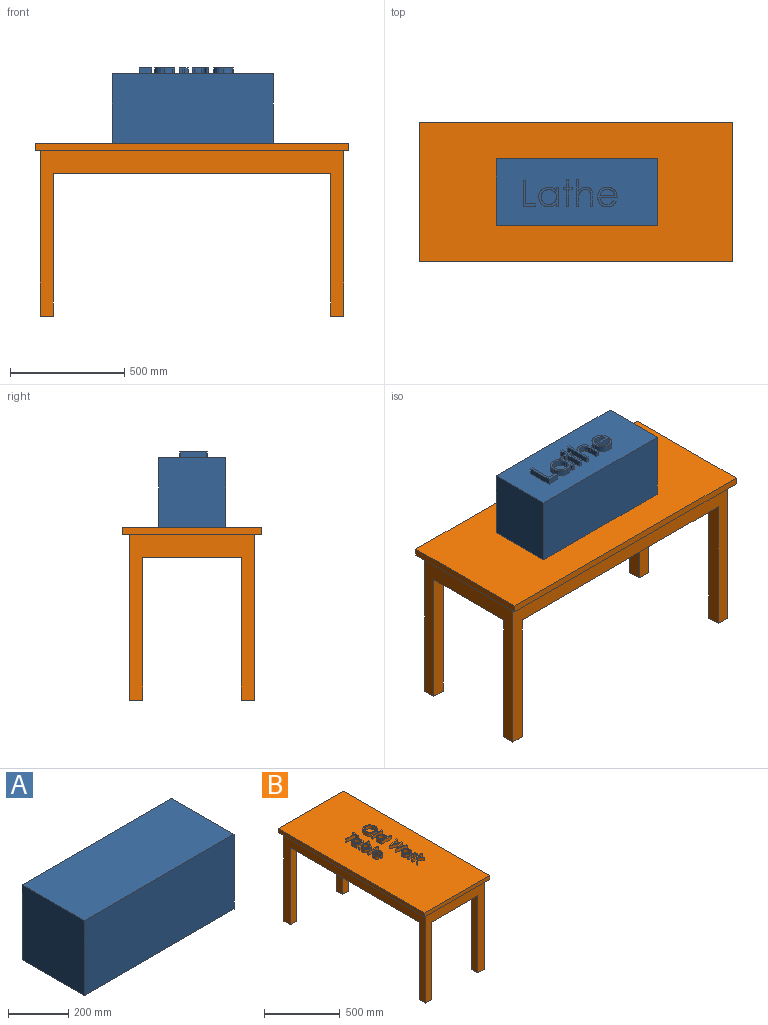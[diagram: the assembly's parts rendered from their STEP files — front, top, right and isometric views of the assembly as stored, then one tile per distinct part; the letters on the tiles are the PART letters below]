
ASSEMBLY  parts=2 mates=1
PART A: 72 faces, bbox 704.9x292.1x330.2 mm
  f0: plane 704.85x292.1mm, normal (0,0,-1), area 189595.3mm2, adj f1,f2,f3,f4,f6,f7,f8,f9
  f1: plane 304.8x292.1mm, normal (-1,0,0), area 89032.1mm2, adj f0,f2,f4,f5
  f2: plane 704.85x304.8mm, normal (0,1,0), area 214838.3mm2, adj f0,f1,f3,f5
  f3: plane 304.8x292.1mm, normal (1,0,0), area 89032.1mm2, adj f0,f2,f4,f5
  f4: plane 704.85x304.8mm, normal (0,-1,0), area 214838.3mm2, adj f0,f1,f3,f5
  f5: plane 704.85x292.1mm, normal (0,0,1), area 205886.7mm2, adj f1,f2,f3,f4
  f6: plane 114.3x25.4mm, normal (-1,0,0), area 2903.2mm2, adj f0,f7,f11,f12
  f7: plane 54.22x25.4mm, normal (0,1,0), area 1377.2mm2, adj f0,f6,f8,f12
  f8: plane 25.4x11.72mm, normal (1,0,0), area 297.8mm2, adj f0,f7,f9,f12
  f9: plane 43.96x25.4mm, normal (0,-1,0), area 1116.6mm2, adj f0,f8,f10,f12
  f10: plane 102.58x25.4mm, normal (1,0,0), area 2605.5mm2, adj f0,f9,f11,f12
  f11: plane 25.4x10.26mm, normal (0,-1,0), area 260.5mm2, adj f0,f6,f10,f12
  f12: plane 114.3x54.22mm, normal (0,0,-1), area 1687.8mm2, adj f6,f7,f8,f9,f10,f11
  f13: plane 87.92x86.46mm, normal (0,0,-1), area 2938.1mm2, adj f14,f15,f16,f17,f18,f19,f20,f21
  f14: plane 25.4x10.26mm, normal (0,-1,0), area 260.5mm2, adj f0,f13,f15,f22
  f15: plane 25.4x15.46mm, normal (-1,0,0), area 392.6mm2, adj f0,f13,f14,f16
  f16: extruded ~33.8x25.4mm, area 1000.4mm2, adj f0,f13,f15,f17
  f17: extruded ~43.87x43mm, area 1735.3mm2, adj f0,f13,f16,f18
  f18: extruded ~43.55x43.46mm, area 1739.5mm2, adj f0,f13,f17,f19
  f19: extruded ~34.12x25.4mm, area 990.3mm2, adj f0,f13,f18,f20
  f20: plane 25.4x14.45mm, normal (-1,0,0), area 367mm2, adj f0,f13,f19,f21
  f21: plane 25.4x10.26mm, normal (0,1,0), area 260.5mm2, adj f0,f13,f20,f22
  f22: plane 83.53x25.4mm, normal (1,0,0), area 2121.6mm2, adj f0,f13,f14,f21
  f23: extruded ~33.66x33.15mm, area 1339.9mm2, adj f13,f24,f26,f27
  f24: extruded ~33.75x32.86mm, area 1330.1mm2, adj f13,f23,f25,f27
  f25: extruded ~33.66x33.09mm, area 1330mm2, adj f13,f24,f26,f27
  f26: extruded ~33.75x32.79mm, area 1333.9mm2, adj f13,f23,f25,f27
  f27: plane 67.41x65.94mm, normal (0,0,-1), area 3508mm2, adj f23,f24,f25,f26
  f28: plane 33.7x25.4mm, normal (-1,0,0), area 856.1mm2, adj f0,f29,f39,f40
  f29: plane 25.4x14.65mm, normal (0,-1,0), area 372.2mm2, adj f0,f28,f30,f40
  f30: plane 25.4x10.26mm, normal (-1,0,0), area 260.5mm2, adj f0,f29,f31,f40
  f31: plane 25.4x14.65mm, normal (0,1,0), area 372.2mm2, adj f0,f30,f32,f40
  f32: plane 73.27x25.4mm, normal (-1,0,0), area 1861mm2, adj f0,f31,f33,f40
  f33: plane 25.4x10.26mm, normal (0,1,0), area 260.5mm2, adj f0,f32,f34,f40
  f34: plane 73.27x25.4mm, normal (1,0,0), area 1861mm2, adj f0,f33,f35,f40
  f35: plane 25.4x14.65mm, normal (0,1,0), area 372.2mm2, adj f0,f34,f36,f40
  f36: plane 25.4x10.26mm, normal (1,0,0), area 260.5mm2, adj f0,f35,f37,f40
  f37: plane 25.4x14.65mm, normal (0,-1,0), area 372.2mm2, adj f0,f36,f38,f40
  f38: plane 33.7x25.4mm, normal (1,0,0), area 856.1mm2, adj f0,f37,f39,f40
  f39: plane 25.4x10.26mm, normal (0,-1,0), area 260.5mm2, adj f0,f28,f38,f40
  f40: plane 117.23x39.57mm, normal (0,0,-1), area 1503.1mm2, adj f28,f29,f30,f31,f32,f33,f34,f35
  f41: plane 117.23x25.4mm, normal (-1,0,0), area 2977.7mm2, adj f0,f42,f54,f55
  f42: plane 25.4x10.26mm, normal (0,1,0), area 260.5mm2, adj f0,f41,f43,f55
  f43: plane 30.2x25.4mm, normal (1,0,0), area 767.1mm2, adj f0,f42,f44,f55
  f44: extruded ~25.4x22.42mm, area 571.9mm2, adj f0,f43,f45,f55
  f45: extruded ~28.39x25.4mm, area 982mm2, adj f0,f44,f46,f55
  f46: extruded ~25.4x21.59mm, area 754mm2, adj f0,f45,f47,f55
  f47: extruded ~25.4x19mm, area 484.5mm2, adj f0,f46,f48,f55
  f48: plane 39.29x25.4mm, normal (-1,0,0), area 998mm2, adj f0,f47,f49,f55
  f49: plane 25.4x10.26mm, normal (0,1,0), area 260.5mm2, adj f0,f48,f50,f55
  f50: plane 42.66x25.4mm, normal (1,0,0), area 1083.5mm2, adj f0,f49,f51,f55
  f51: extruded ~42.34x31.23mm, area 1525.1mm2, adj f0,f50,f52,f55
  f52: extruded ~31.78x25.4mm, area 954mm2, adj f0,f51,f53,f55
  f53: plane 49.48x25.4mm, normal (1,0,0), area 1256.8mm2, adj f0,f52,f54,f55
  f54: plane 25.4x10.26mm, normal (0,-1,0), area 260.5mm2, adj f0,f41,f53,f55
  f55: plane 117.23x73.27mm, normal (0,0,-1), area 2548.4mm2, adj f41,f42,f43,f44,f45,f46,f47,f48
  f56: plane 86.46x84.99mm, normal (0,0,-1), area 2916.5mm2, adj f57,f58,f59,f60,f61,f62,f63,f64
  f57: extruded ~30.75x25.4mm, area 944.5mm2, adj f0,f56,f58,f66
  f58: extruded ~30.77x30.48mm, area 1227.5mm2, adj f0,f56,f57,f59
  f59: plane 74.73x25.4mm, normal (0,1,0), area 1898.3mm2, adj f0,f56,f58,f60
  f60: extruded ~28.99x25.4mm, area 785.7mm2, adj f0,f56,f59,f61
  f61: extruded ~33.64x25.4mm, area 988.3mm2, adj f0,f56,f60,f62
  f62: extruded ~32.65x25.4mm, area 953.8mm2, adj f0,f56,f61,f63
  f63: extruded ~27.89x25.4mm, area 763.9mm2, adj f0,f56,f62,f64
  f64: extruded ~43x42.02mm, area 1708.4mm2, adj f0,f56,f63,f65
  f65: extruded ~38.58x25.4mm, area 1206.5mm2, adj f0,f56,f64,f66
  f66: plane 25.4x9.11mm, normal (0.46,-0.89,0), area 261.4mm2, adj f0,f56,f57,f65
  f67: plane 63.4x25.4mm, normal (0,-1,0), area 1610.4mm2, adj f56,f68,f70,f71
  f68: extruded ~31.94x25.4mm, area 1117.1mm2, adj f56,f67,f69,f71
  f69: extruded ~25.4x21.52mm, area 595.1mm2, adj f56,f68,f70,f71
  f70: extruded ~25.4x17.08mm, area 508.8mm2, adj f56,f67,f69,f71
  f71: plane 63.4x24.91mm, normal (0,0,-1), area 1189.4mm2, adj f67,f68,f69,f70
PART B: 163 faces, bbox 609.9x1371.7x781.1 mm
  f0: plane 1371.73x609.89mm, normal (0,0,1), area 803903mm2, adj f10,f11,f12,f13,f24,f25,f26,f27
  f1: plane 1371.73x609.89mm, normal (0,0,-1), area 111370.7mm2, adj f10,f11,f12,f13,f14,f15,f17,f19
  f2: plane 625.48x57.15mm, normal (1,0,0), area 35745.9mm2, adj f3,f14,f16,f22
  f3: plane 625.48x57.15mm, normal (0,-1,0), area 35745.9mm2, adj f2,f15,f16,f22
  f4: plane 625.48x57.15mm, normal (0,-1,0), area 35745.9mm2, adj f5,f17,f18,f22
  f5: plane 625.48x57.15mm, normal (-1,0,0), area 35745.9mm2, adj f4,f14,f18,f22
  f6: plane 625.48x57.15mm, normal (-1,0,0), area 35745.9mm2, adj f7,f19,f20,f22
  f7: plane 625.48x57.15mm, normal (0,1,0), area 35745.9mm2, adj f6,f17,f20,f22
  f8: plane 625.48x57.15mm, normal (0,1,0), area 35745.9mm2, adj f9,f15,f21,f22
  f9: plane 625.48x57.15mm, normal (1,0,0), area 35745.9mm2, adj f8,f19,f21,f22
  f10: plane 609.6x31.75mm, normal (0,1,0), area 19354.8mm2, adj f0,f1,f11,f13
  f11: plane 1371.6x31.75mm, normal (-1,0,0), area 43548.3mm2, adj f0,f1,f10,f12
  f12: plane 609.6x31.75mm, normal (0,-1,0), area 19354.8mm2, adj f0,f1,f11,f13
  f13: plane 1371.6x31.75mm, normal (1,0,0), area 43548.3mm2, adj f0,f1,f10,f12
  f14: plane 723.9x546.1mm, normal (0,1,0), area 125241.7mm2, adj f1,f2,f5,f15,f16,f17,f18,f22
  f15: plane 1327.15x723.9mm, normal (-1,0,0), area 202116.5mm2, adj f1,f3,f8,f14,f16,f19,f21,f22
  f16: plane 57.16x57.16mm, normal (0,0,-1), area 3266.1mm2, adj f2,f3,f14,f15
  f17: plane 1327.15x723.9mm, normal (1,0,0), area 202116.5mm2, adj f1,f4,f7,f14,f18,f19,f20,f22
  f18: plane 57.16x57.16mm, normal (0,0,-1), area 3266.1mm2, adj f4,f5,f14,f17
  f19: plane 723.9x546.1mm, normal (0,-1,0), area 125241.7mm2, adj f1,f6,f9,f15,f17,f20,f21,f22
  f20: plane 57.16x57.16mm, normal (0,0,-1), area 3266.1mm2, adj f6,f7,f17,f19
  f21: plane 57.16x57.16mm, normal (0,0,-1), area 3266.1mm2, adj f8,f9,f15,f19
  f22: plane 1327.24x546.36mm, normal (0,0,-1), area 711692.1mm2, adj f2,f3,f4,f5,f6,f7,f8,f9
  f23: plane 93.46x93.46mm, normal (0,0,1), area 2301.1mm2, adj f24,f25,f26,f27,f28,f29,f30,f31
  f24: extruded ~47.13x46.15mm, area 1864.4mm2, adj f0,f23,f25,f27
  f25: extruded ~46.88x46.33mm, area 1865mm2, adj f0,f23,f24,f26
  f26: extruded ~46.78x46.58mm, area 1868mm2, adj f0,f23,f25,f27
  f27: extruded ~47.31x46.68mm, area 1884.7mm2, adj f0,f23,f24,f26
  f28: extruded ~38.94x37.55mm, area 1529.2mm2, adj f23,f29,f31,f32
  f29: extruded ~38.57x37.98mm, area 1529.4mm2, adj f23,f28,f30,f32
  f30: extruded ~38.58x37.25mm, area 1516.9mm2, adj f23,f29,f31,f32
  f31: extruded ~38.92x37.67mm, area 1535.2mm2, adj f23,f28,f30,f32
  f32: plane 77.5x75.22mm, normal (0,0,1), area 4603.4mm2, adj f28,f29,f30,f31
  f33: plane 91.18x25.4mm, normal (0,1,0), area 2316mm2, adj f0,f34,f36,f37
  f34: plane 25.4x7.98mm, normal (-1,0,0), area 202.6mm2, adj f0,f33,f35,f37
  f35: plane 91.18x25.4mm, normal (0,-1,0), area 2316mm2, adj f0,f34,f36,f37
  f36: plane 25.4x7.98mm, normal (1,0,0), area 202.6mm2, adj f0,f33,f35,f37
  f37: plane 91.18x8mm, normal (0,0,1), area 727.4mm2, adj f33,f34,f35,f36
  f38: plane 92.33x68.39mm, normal (0,0,1), area 1979.8mm2, adj f39,f40,f41,f42,f43,f44,f45,f46
  f39: plane 25.4x7.98mm, normal (1,0,0), area 202.6mm2, adj f0,f38,f40,f47
  f40: plane 38.79x25.4mm, normal (0,1,0), area 985.2mm2, adj f0,f38,f39,f41
  f41: extruded ~26.29x25.4mm, area 784.2mm2, adj f0,f38,f40,f42
  f42: extruded ~34.11x33.45mm, area 1349.6mm2, adj f0,f38,f41,f43
  f43: extruded ~33.88x33.79mm, area 1353mm2, adj f0,f38,f42,f44
  f44: extruded ~26.53x25.4mm, area 770.2mm2, adj f0,f38,f43,f45
  f45: plane 25.4x11.24mm, normal (0,1,0), area 285.4mm2, adj f0,f38,f44,f46
  f46: plane 25.4x7.98mm, normal (-1,0,0), area 202.6mm2, adj f0,f38,f45,f47
  f47: plane 91.18x25.4mm, normal (0,-1,0), area 2316mm2, adj f0,f38,f39,f46
  f48: extruded ~26.18x25.78mm, area 1042.2mm2, adj f38,f49,f51,f52
  f49: extruded ~26.24x25.56mm, area 1034.5mm2, adj f38,f48,f50,f52
  f50: extruded ~26.18x25.73mm, area 1034.4mm2, adj f38,f49,f51,f52
  f51: extruded ~26.24x25.51mm, area 1037.5mm2, adj f38,f48,f50,f52
  f52: plane 52.43x51.29mm, normal (0,0,1), area 2122.1mm2, adj f48,f49,f50,f51
  f53: plane 88.9x25.4mm, normal (-0.26,0.97,0), area 2336.6mm2, adj f0,f54,f65,f66
  f54: plane 25.4x1.14mm, normal (-1,0,0), area 28.9mm2, adj f0,f53,f55,f66
  f55: plane 68x27.05mm, normal (-0.37,-0.93,0), area 1858.8mm2, adj f0,f54,f56,f66
  f56: plane 67.99x26.76mm, normal (-0.37,0.93,0), area 1855.9mm2, adj f0,f55,f57,f66
  f57: plane 25.4x1.14mm, normal (-1,0,0), area 28.9mm2, adj f0,f56,f58,f66
  f58: plane 88.91x25.4mm, normal (-0.26,-0.97,0), area 2338.7mm2, adj f0,f57,f59,f66
  f59: plane 25.4x8.16mm, normal (1,0,0), area 207.2mm2, adj f0,f58,f60,f66
  f60: plane 64.76x25.4mm, normal (0.26,0.97,0), area 1703.6mm2, adj f0,f59,f61,f66
  f61: plane 64.75x25.41mm, normal (0.37,-0.93,0), area 1766.7mm2, adj f0,f60,f62,f66
  f62: plane 25.4x1.16mm, normal (1,0,0), area 29.4mm2, adj f0,f61,f63,f66
  f63: plane 65.2x25.86mm, normal (0.37,0.93,0), area 1781.7mm2, adj f0,f62,f64,f66
  f64: plane 65.19x25.4mm, normal (0.26,-0.97,0), area 1714mm2, adj f0,f63,f65,f66
  f65: plane 25.4x8.25mm, normal (1,0,0), area 209.4mm2, adj f0,f53,f64,f66
  f66: plane 103.72x88.92mm, normal (0,0,1), area 2475.1mm2, adj f53,f54,f55,f56,f57,f58,f59,f60
  f67: plane 67.25x67.25mm, normal (0,0,1), area 1502.1mm2, adj f68,f69,f70,f71,f72,f73,f74,f75
  f68: extruded ~25.4x24.75mm, area 707.2mm2, adj f0,f67,f69,f73
  f69: extruded ~25.4x23.05mm, area 642.9mm2, adj f0,f67,f68,f70
  f70: extruded ~33.67x33.44mm, area 1344.2mm2, adj f0,f67,f69,f71
  f71: extruded ~33.58x33.45mm, area 1342.5mm2, adj f0,f67,f70,f72
  f72: extruded ~25.4x23.1mm, area 644.2mm2, adj f0,f67,f71,f73
  f73: extruded ~25.4x24.69mm, area 704.8mm2, adj f0,f67,f68,f72
  f74: extruded ~25.87x25.65mm, area 1028.6mm2, adj f67,f75,f77,f78
  f75: extruded ~25.88x25.64mm, area 1028.9mm2, adj f67,f74,f76,f78
  f76: extruded ~25.65x25.41mm, area 1022.3mm2, adj f67,f75,f77,f78
  f77: extruded ~25.64x25.42mm, area 1022.2mm2, adj f67,f74,f76,f78
  f78: plane 51.29x51.29mm, normal (0,0,1), area 2075.1mm2, adj f74,f75,f76,f77
  f79: plane 64.97x25.4mm, normal (0,1,0), area 1650.1mm2, adj f0,f80,f89,f90
  f80: plane 25.4x7.98mm, normal (-1,0,0), area 202.6mm2, adj f0,f79,f81,f90
  f81: plane 25.4x21.83mm, normal (0,-1,0), area 554.6mm2, adj f0,f80,f82,f90
  f82: extruded ~25.4x22.3mm, area 568.5mm2, adj f0,f81,f83,f90
  f83: extruded ~25.4x14mm, area 519.5mm2, adj f0,f82,f84,f90
  f84: extruded ~25.4x4.08mm, area 108.5mm2, adj f0,f83,f85,f90
  f85: plane 25.4x6.91mm, normal (-0.54,-0.84,0), area 207.8mm2, adj f0,f84,f86,f90
  f86: extruded ~25.4x6.95mm, area 187.5mm2, adj f0,f85,f87,f90
  f87: extruded ~25.4x15.85mm, area 508.3mm2, adj f0,f86,f88,f90
  f88: plane 25.4x9.56mm, normal (0,-1,0), area 242.9mm2, adj f0,f87,f89,f90
  f89: plane 25.4x7.98mm, normal (1,0,0), area 202.6mm2, adj f0,f79,f88,f90
  f90: plane 66.11x30.77mm, normal (0,0,1), area 711.5mm2, adj f79,f80,f81,f82,f83,f84,f85,f86
  f91: plane 91.18x25.4mm, normal (0,1,0), area 2316mm2, adj f0,f92,f101,f102
  f92: plane 25.4x7.98mm, normal (-1,0,0), area 202.6mm2, adj f0,f91,f93,f102
  f93: plane 29.94x25.4mm, normal (0,-1,0), area 760.4mm2, adj f0,f92,f94,f102
  f94: plane 33.01x29.93mm, normal (-0.74,0.67,0), area 1131.7mm2, adj f0,f93,f95,f102
  f95: plane 25.4x11.45mm, normal (-1,0,0), area 290.9mm2, adj f0,f94,f96,f102
  f96: plane 37.73x34.18mm, normal (0.74,-0.67,0), area 1293.1mm2, adj f0,f95,f97,f102
  f97: plane 34.29x30.78mm, normal (-0.74,-0.67,0), area 1170.4mm2, adj f0,f96,f98,f102
  f98: plane 25.4x11.47mm, normal (1,0,0), area 291.3mm2, adj f0,f97,f99,f102
  f99: plane 29.56x26.51mm, normal (0.74,0.67,0), area 1008.4mm2, adj f0,f98,f100,f102
  f100: plane 52.71x25.4mm, normal (0,-1,0), area 1338.9mm2, adj f0,f99,f101,f102
  f101: plane 25.4x7.98mm, normal (1,0,0), area 202.6mm2, adj f0,f91,f100,f102
  f102: plane 91.18x52.45mm, normal (0,0,1), area 1451.7mm2, adj f91,f92,f93,f94,f95,f96,f97,f98
  f103: plane 25.4x19.38mm, normal (-1,0,0), area 492.1mm2, adj f0,f104,f110,f111
  f104: plane 79.78x25.4mm, normal (0,1,0), area 2026.5mm2, adj f0,f103,f105,f111
  f105: plane 25.4x7.98mm, normal (-1,0,0), area 202.6mm2, adj f0,f104,f106,f111
  f106: plane 79.78x25.4mm, normal (0,-1,0), area 2026.5mm2, adj f0,f105,f107,f111
  f107: plane 25.4x19.38mm, normal (-1,0,0), area 492.1mm2, adj f0,f106,f108,f111
  f108: plane 25.4x9.12mm, normal (0,-1,0), area 231.6mm2, adj f0,f107,f109,f111
  f109: plane 46.73x25.4mm, normal (1,0,0), area 1186.9mm2, adj f0,f108,f110,f111
  f110: plane 25.4x9.12mm, normal (0,1,0), area 231.6mm2, adj f0,f103,f109,f111
  f111: plane 88.91x46.73mm, normal (0,0,1), area 1062.6mm2, adj f103,f104,f105,f106,f107,f108,f109,f110
  f112: plane 68.39x67.25mm, normal (0,0,1), area 1777.4mm2, adj f113,f114,f115,f116,f117,f118,f119,f120
  f113: plane 25.4x7.98mm, normal (1,0,0), area 202.6mm2, adj f0,f112,f114,f121
  f114: plane 25.4x12.02mm, normal (0,1,0), area 305.3mm2, adj f0,f112,f113,f115
  f115: extruded ~26.29x25.4mm, area 778.1mm2, adj f0,f112,f114,f116
  f116: extruded ~34.11x33.45mm, area 1349.6mm2, adj f0,f112,f115,f117
  f117: extruded ~33.88x33.79mm, area 1353mm2, adj f0,f112,f116,f118
  f118: extruded ~26.53x25.4mm, area 770.2mm2, adj f0,f112,f117,f119
  f119: plane 25.4x11.24mm, normal (0,1,0), area 285.4mm2, adj f0,f112,f118,f120
  f120: plane 25.4x7.98mm, normal (-1,0,0), area 202.6mm2, adj f0,f112,f119,f121
  f121: plane 64.97x25.4mm, normal (0,-1,0), area 1650.1mm2, adj f0,f112,f113,f120
  f122: extruded ~26.18x25.78mm, area 1042.2mm2, adj f112,f123,f125,f126
  f123: extruded ~26.24x25.56mm, area 1034.5mm2, adj f112,f122,f124,f126
  f124: extruded ~26.18x25.73mm, area 1034.4mm2, adj f112,f123,f125,f126
  f125: extruded ~26.24x25.51mm, area 1037.5mm2, adj f112,f122,f124,f126
  f126: plane 52.43x51.29mm, normal (0,0,1), area 2122.1mm2, adj f122,f123,f124,f125
  f127: plane 92.31x68.4mm, normal (0,0,1), area 1980.4mm2, adj f128,f129,f130,f131,f132,f133,f134,f135
  f128: plane 25.4x7.98mm, normal (-1,0,0), area 202.6mm2, adj f0,f127,f129,f136
  f129: plane 25.4x12.02mm, normal (0,-1,0), area 305.3mm2, adj f0,f127,f128,f130
  f130: extruded ~26.25x25.4mm, area 776.9mm2, adj f0,f127,f129,f131
  f131: extruded ~34.15x33.51mm, area 1351.6mm2, adj f0,f127,f130,f132
  f132: extruded ~33.91x33.74mm, area 1352.4mm2, adj f0,f127,f131,f133
  f133: extruded ~26.5x25.4mm, area 775.8mm2, adj f0,f127,f132,f134
  f134: plane 38x25.4mm, normal (0,-1,0), area 965.3mm2, adj f0,f127,f133,f135
  f135: plane 25.4x7.98mm, normal (1,0,0), area 202.6mm2, adj f0,f127,f134,f136
  f136: plane 91.18x25.4mm, normal (0,1,0), area 2316mm2, adj f0,f127,f128,f135
  f137: extruded ~26.18x25.76mm, area 1042mm2, adj f127,f138,f140,f141
  f138: extruded ~26.24x25.53mm, area 1033.6mm2, adj f127,f137,f139,f141
  f139: extruded ~26.13x25.76mm, area 1033.9mm2, adj f127,f138,f140,f141
  f140: extruded ~26.3x25.53mm, area 1038.3mm2, adj f127,f137,f139,f141
  f141: plane 52.43x51.29mm, normal (0,0,1), area 2121.3mm2, adj f137,f138,f139,f140
  f142: plane 91.18x25.4mm, normal (0,1,0), area 2316mm2, adj f0,f143,f145,f146
  f143: plane 25.4x7.98mm, normal (-1,0,0), area 202.6mm2, adj f0,f142,f144,f146
  f144: plane 91.18x25.4mm, normal (0,-1,0), area 2316mm2, adj f0,f143,f145,f146
  f145: plane 25.4x7.98mm, normal (1,0,0), area 202.6mm2, adj f0,f142,f144,f146
  f146: plane 91.18x8mm, normal (0,0,1), area 727.4mm2, adj f142,f143,f144,f145
  f147: plane 67.25x66.11mm, normal (0,0,1), area 1764.3mm2, adj f148,f149,f150,f151,f152,f153,f154,f155
  f148: extruded ~25.4x23.91mm, area 734.6mm2, adj f0,f147,f149,f157
  f149: extruded ~25.4x23.93mm, area 954.7mm2, adj f0,f147,f148,f150
  f150: plane 58.13x25.4mm, normal (-1,0,0), area 1476.4mm2, adj f0,f147,f149,f151
  f151: extruded ~25.4x22.54mm, area 611.1mm2, adj f0,f147,f150,f152
  f152: extruded ~26.16x25.4mm, area 768.7mm2, adj f0,f147,f151,f153
  f153: extruded ~25.4x25.39mm, area 741.9mm2, adj f0,f147,f152,f154
  f154: extruded ~25.4x21.69mm, area 594.2mm2, adj f0,f147,f153,f155
  f155: extruded ~33.44x32.69mm, area 1328.8mm2, adj f0,f147,f154,f156
  f156: extruded ~30x25.4mm, area 938.4mm2, adj f0,f147,f155,f157
  f157: plane 25.4x7.09mm, normal (0.89,-0.46,0), area 203.3mm2, adj f0,f147,f148,f156
  f158: plane 49.31x25.4mm, normal (1,0,0), area 1252.5mm2, adj f147,f159,f161,f162
  f159: extruded ~25.4x24.85mm, area 868.8mm2, adj f147,f158,f160,f162
  f160: extruded ~25.4x16.74mm, area 462.8mm2, adj f147,f159,f161,f162
  f161: extruded ~25.4x13.29mm, area 395.8mm2, adj f147,f158,f160,f162
  f162: plane 49.31x19.38mm, normal (0,0,1), area 719.5mm2, adj f158,f159,f160,f161
PLACE A rot(axis=(1,0,0),180deg) t=(-2029.5,-7918.88,-1576.36)mm
PLACE B rot(axis=(0,0,1),90deg) t=(563.28,-4719.83,1233.86)mm
MATE fastened A.f5 <-> B.f0  axis (0,0,-1) through (1196.78,-3202.68,-323.65)mm
